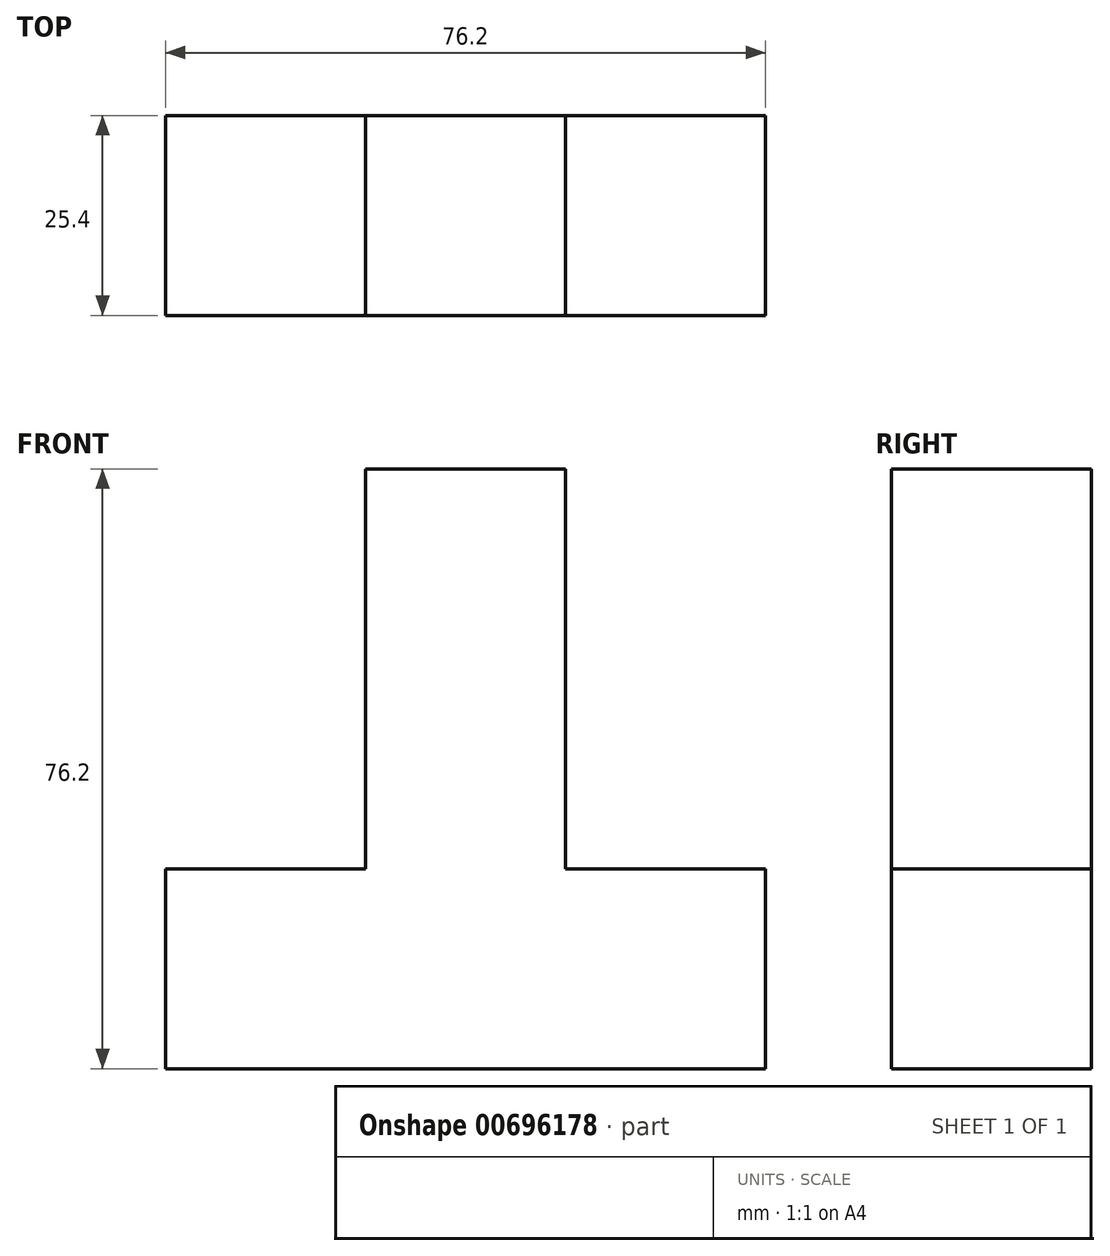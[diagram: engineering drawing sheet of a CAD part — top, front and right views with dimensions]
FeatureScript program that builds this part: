
annotation { "Feature Type Name" : "Feature", "Feature Type Description" : "" }
export const myFeature = defineFeature(function(context is Context, id is Id, definition is map)
    precondition{}
    {
        {
            var Q0;
            Q0=qCreatedBy(makeId("Front.planeOp"),FACE);
            var sketch = newSketch(context, id + "F0", { "sketchPlane" : qUnion([Q0])});
            skLineSegment(sketch, "E0", {"start": v(-50.8, 25.4) * mm, "end": v(-50.8, 0) * mm});
            skLineSegment(sketch, "E1", {"start": v(-50.8, 0) * mm, "end": v(25.4, 0) * mm});
            skLineSegment(sketch, "E2", {"start": v(25.4, 0) * mm, "end": v(25.4, 25.4) * mm});
            skLineSegment(sketch, "E3", {"start": v(25.4, 25.4) * mm, "end": v(0, 25.4) * mm});
            skLineSegment(sketch, "E4", {"start": v(-50.8, 25.4) * mm, "end": v(-25.4, 25.4) * mm});
            skLineSegment(sketch, "E5", {"start": v(0, 25.4) * mm, "end": v(0, 76.2) * mm});
            skLineSegment(sketch, "E6", {"start": v(-25.4, 25.4) * mm, "end": v(-25.4, 76.2) * mm});
            skLineSegment(sketch, "E7", {"start": v(-25.4, 76.2) * mm, "end": v(0, 76.2) * mm});
            skSolve(sketch);
        }
        {
            var Q0;
            Q0 = qSketchRegion(id + "F0", true);
            extrude(context, id + "F1", {"entities" : qUnion([Q0]), "depth" : 25.4 * mm, "offsetDistance" : 25.4 * mm});
        }
    });
